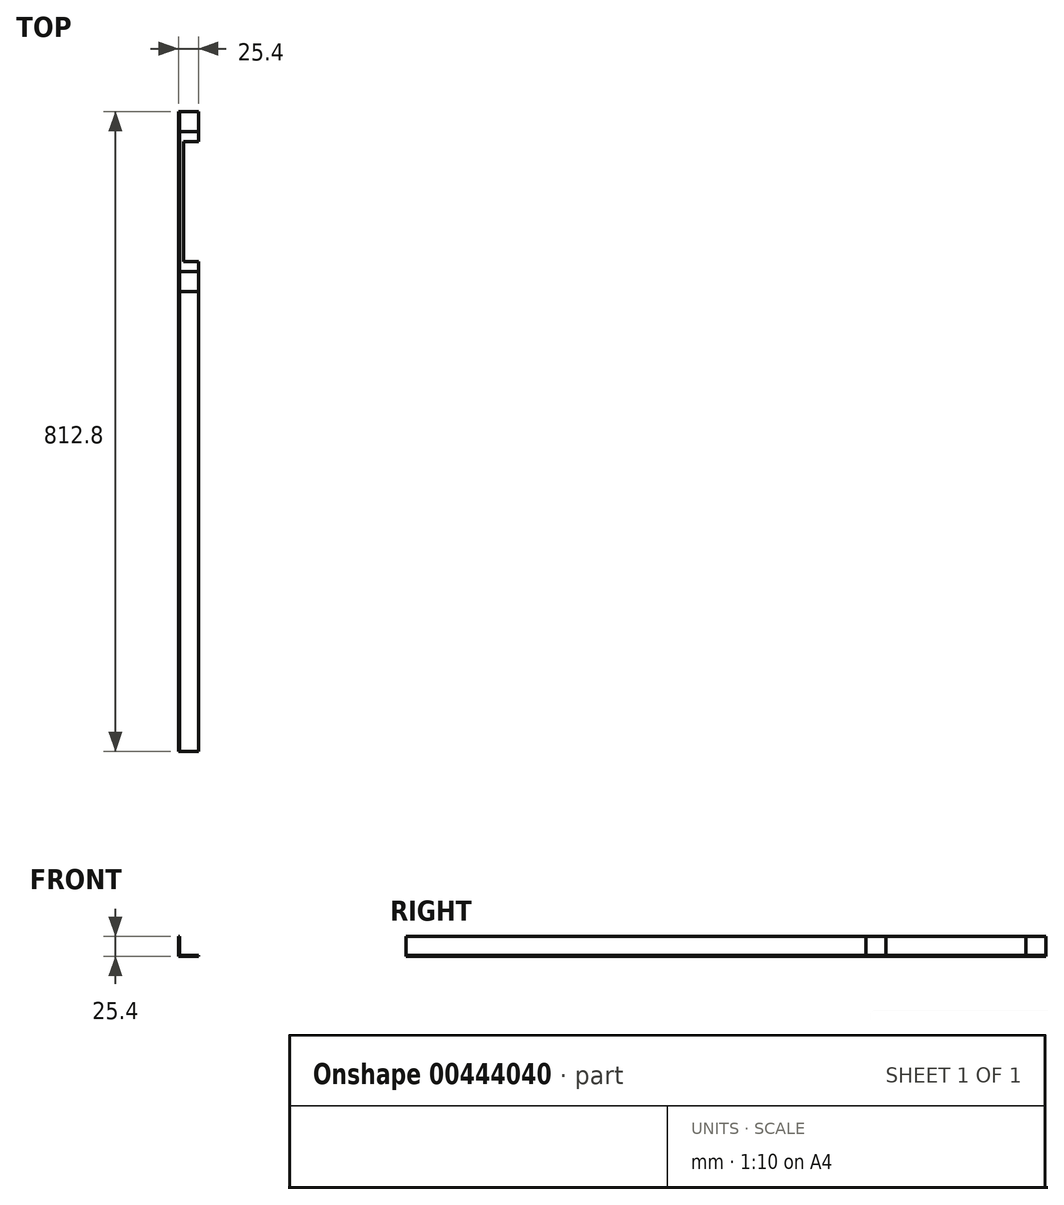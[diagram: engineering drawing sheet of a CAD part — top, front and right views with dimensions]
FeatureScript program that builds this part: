
annotation { "Feature Type Name" : "Feature", "Feature Type Description" : "" }
export const myFeature = defineFeature(function(context is Context, id is Id, definition is map)
    precondition{}
    {
        {
            var Q0;
            Q0=qCreatedBy(makeId("Front.planeOp"),FACE);
            var sketch = newSketch(context, id + "F0", { "sketchPlane" : qUnion([Q0])});
            skLineSegment(sketch, "E0", {"start": v(0, 0) * mm, "end": v(0, 25.4) * mm});
            skLineSegment(sketch, "E1", {"start": v(0, 25.4) * mm, "end": v(1.59, 25.4) * mm});
            skLineSegment(sketch, "E2", {"start": v(1.59, 25.4) * mm, "end": v(1.59, 1.59) * mm});
            skLineSegment(sketch, "E3", {"start": v(1.59, 1.59) * mm, "end": v(25.4, 1.59) * mm});
            skLineSegment(sketch, "E4", {"start": v(25.4, 1.59) * mm, "end": v(25.4, 0) * mm});
            skLineSegment(sketch, "E5", {"start": v(25.4, 0) * mm, "end": v(0, 0) * mm});
            skSolve(sketch);
        }
        {
            var Q0;
            Q0=makeQuery(id+"F0.imprint","IMPRINT",FACE,{"disambiguationData":[TD([[makeQuery(id+"F0.imprint","IMPRINT",EDGE,{"derivedFrom":sQuery(id+"F0.wireOp",EDGE,"E0")}),-1.0]])]});
            extrude(context, id + "F1", {"entities" : qUnion([Q0]), "depth" : 203.2 * mm});
        }
        {
            var Q0;
            Q0=qSketchRegion(id+"F0",true);
            extrude(context, id + "F2", {"entities" : qUnion([Q0]), "depth" : 812.8 * mm});
        }
        {
            var Q0;
            Q0=qSketchRegion(id+"F0",true);
            extrude(context, id + "F3", {"entities" : qUnion([Q0]), "depth" : 25.4 * mm});
        }
        {
            var Q0;
            Q0=qSketchRegion(id+"F0",true);
            extrude(context, id + "F4", {"entities" : qUnion([Q0]), "depth" : 228.6 * mm});
        }
        {
            var Q0;
            Q0=makeQuery(id+"F4.opExtrude","SWEPT_FACE",FACE,{"disambiguationData":[OSD([sQuery(id+"F0.wireOp",EDGE,"E3")])]});
            var sketch = newSketch(context, id + "F5", { "sketchPlane" : qUnion([Q0])});
            skLineSegment(sketch, "E6", {"start": v(25.4, -38.1) * mm, "end": v(6.35, -38.1) * mm});
            skLineSegment(sketch, "E7", {"start": v(6.35, -38.1) * mm, "end": v(6.35, -190.5) * mm});
            skLineSegment(sketch, "E8", {"start": v(6.35, -190.5) * mm, "end": v(25.4, -190.5) * mm});
            skLineSegment(sketch, "E9", {"start": v(25.4, -38.1) * mm, "end": v(25.4, -190.5) * mm});
            skSolve(sketch);
        }
        {
            var Q0;
            Q0=makeQuery(id+"F5.imprint","IMPRINT",FACE,{"disambiguationData":[TD([[makeQuery(id+"F5.imprint","IMPRINT",EDGE,{"derivedFrom":sQuery(id+"F5.wireOp",EDGE,"E6")}),1.0]])]});
            extrude(context, id + "F6", {"entities" : qUnion([Q0]), "operationType" : NewBodyOperationType.REMOVE, "oppositeDirection" : true, "depth" : 25.4 * mm});
        }
    });
